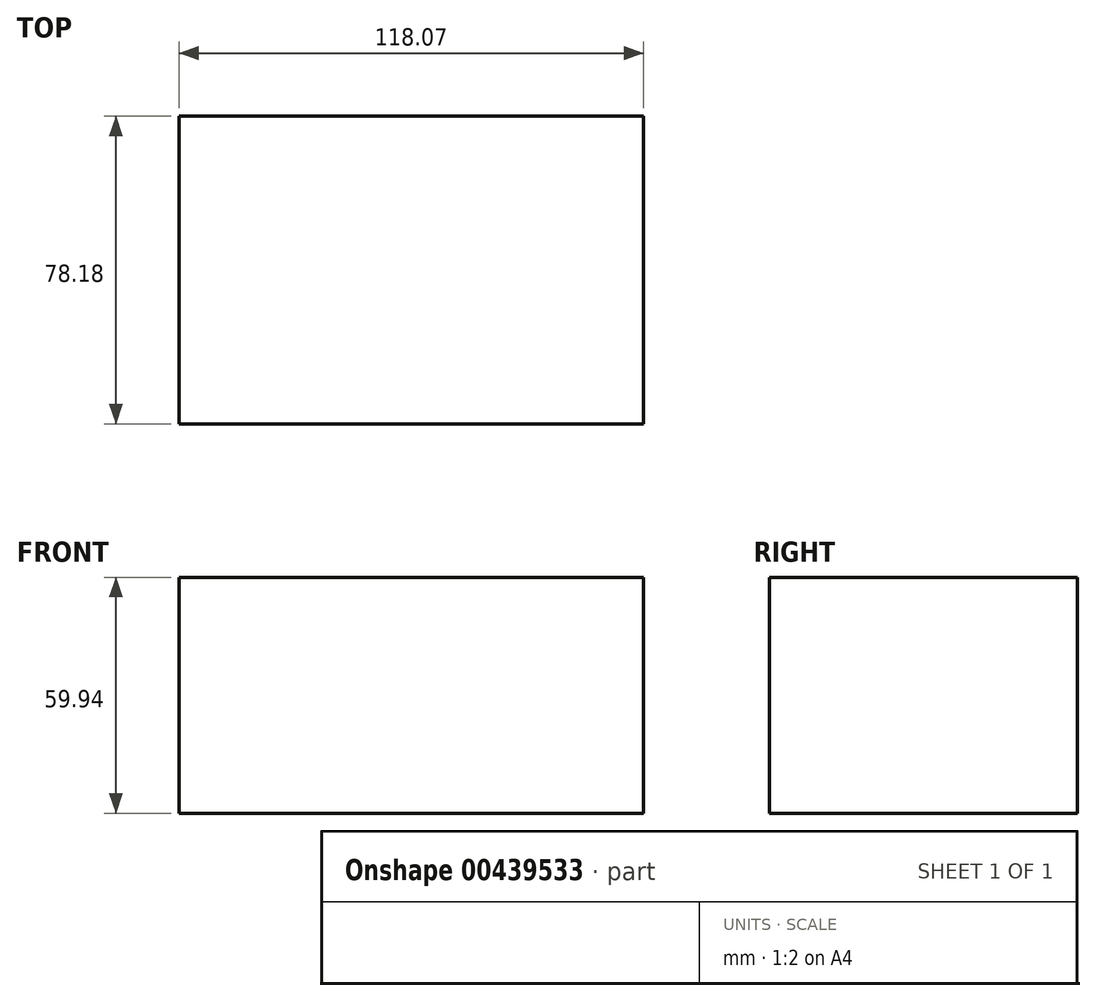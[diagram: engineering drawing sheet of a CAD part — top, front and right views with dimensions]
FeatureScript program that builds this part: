
annotation { "Feature Type Name" : "Feature", "Feature Type Description" : "" }
export const myFeature = defineFeature(function(context is Context, id is Id, definition is map)
    precondition{}
    {
        {
            var Q0;
            Q0=qCreatedBy(makeId("Top.planeOp"),FACE);
            var sketch = newSketch(context, id + "F0", { "sketchPlane" : qUnion([Q0])});
            skLineSegment(sketch, "E0.bottom", {"start": v(67.08, -39.09) * mm, "end": v(-50.99, -39.09) * mm});
            skLineSegment(sketch, "E0.top", {"start": v(67.08, 39.09) * mm, "end": v(-50.99, 39.09) * mm});
            skLineSegment(sketch, "E0.left", {"start": v(67.08, -39.09) * mm, "end": v(67.08, 39.09) * mm});
            skLineSegment(sketch, "E0.right", {"start": v(-50.99, -39.09) * mm, "end": v(-50.99, 39.09) * mm});
            skPoint(sketch, "E0.middle", {"position": v(8.05, 0) * mm});
            skSolve(sketch);
        }
        {
            var Q0;
            Q0=makeQuery(id+"F0.imprint","IMPRINT",FACE,{"disambiguationData":[TD([[makeQuery(id+"F0.imprint","IMPRINT",EDGE,{"derivedFrom":sQuery(id+"F0.wireOp",EDGE,"E0.bottom")}),-1.0]])]});
            extrude(context, id + "F1", {"entities" : qUnion([Q0]), "depth" : 59.94 * mm});
        }
    });
